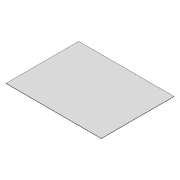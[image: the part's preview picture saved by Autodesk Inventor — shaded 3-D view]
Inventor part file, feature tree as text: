
AUTODESK INVENTOR PART (.ipt)
format: ipt  version: 2021 (Build 250183000, 183)  size: 73,216 bytes
history: native  units: in
note: dims shown in document units (in); Inventor stores cm internally (conversion verified against a paired STEP export)
features: extrude x1, sketch x1
ambient origin geometry x8: Origin, YZ Plane, XZ Plane, XY Plane, X Axis, Y Axis, Z Axis, Center Point
bodies: Solid1 (feature_tree)
feature tree (2):
  extrude  "Extrusion1"  [1 undecoded]
  sketch  "Sketch1"  dims[d2=0.063in d3=0.0in]
note: 1 required parameter value undecoded (feature->parameter linkage not recoverable at this tier; creation-order binding heuristic only, values carry confidence <= 0.55)
